# Revit family: 4C-6_Door_High_Units_FL.rfa
name_source: partatom
category: Specialty Equipment
revit_build: Autodesk Revit 2016 (Build: 20150714_1515(x64)
units: mm (PartAtom-declared; Revit-internal decimal feet)

## family parameters
Always vertical = Yes
Cut with Voids When Loaded = No
Host = Wall
Part Type = Normal
Room Calculation Point = No
Round Connector Dimension = Use Diameter
Shared = No

## types (13) — shared parameters
Assembly Code = C1030910
Back Enclosure Material = Aluminum - Salsbury Finish = Anodized
Depth = 17.025"
Door Slot R3 = 3700 Series 4C Door Configurations : Empty
Height = 23.470"
Latch Locks - Left Side = No
Latch Locks - Right Side = No
Lock Material = Stainless Steel -Salsbury Finish =  Polished
Manufacturer = Salsbury Industries
MasterFormat Number = 10 55 00
MasterFormat Title = Postal Specialties
Version = 2.0 (08/09/16)

## per-type parameters (varying)
| type | Bottom Back Plate | Description | Door Slot L1 | Door Slot L2 | Door Slot L3 | Door Slot L4 | Door Slot L5 | Door Slot L6 | Door Slot R1 | Door Slot R2 | Door Slot R4 | Door Slot R5 | Door Slot R6 | Latch Alignment | Left Inside Wall | Right Inside Wall | Top Back Plate | Type Comments | Vertical Center Divider | Width |
| 3706D-10 FL | Yes | 6 Door High Unit: 10 MB1, OM2 | 3700 Series 4C Door Configurations : MB1 Door | 3700 Series 4C Door Configurations : MB1 Door w/ Divider | 3700 Series 4C Door Configurations : MB1 Door w/ Divider | 3700 Series 4C Door Configurations : MB1 Door w/ Divider | 3700 Series 4C Door Configurations : MB1 Door w/ Divider | 3700 Series 4C Door Configurations : MB1 Door w/ Divider | 3700 Series 4C Door Configurations : MB1 Door | 3700 Series 4C Door Configurations : MB1 Door w/ Divider | 3700 Series 4C OM2 Configuration : OM2-FL | 3700 Series 4C Door Configurations : MB1 Door w/ Divider | 3700 Series 4C Door Configurations : MB1 Door w/ Divider | 14.857" | Yes | Yes | Yes | 4C Standard Horizontal Mailbox - Front Loading | Yes | 31.098" |
| 3706S-04 FL | No | 6 Door High Unit: 4 MB1, OM2 | 3700 Series 4C Door Configurations : Empty | 3700 Series 4C Door Configurations : Empty | 3700 Series 4C Door Configurations : Empty | 3700 Series 4C Door Configurations : Empty | 3700 Series 4C Door Configurations : Empty | 3700 Series 4C Door Configurations : Empty | 3700 Series 4C Door Configurations : MB1 Door | 3700 Series 4C Door Configurations : MB1 Door w/ Divider | 3700 Series 4C OM2 Configuration : OM2-FL | 3700 Series 4C Door Configurations : MB1 Door w/ Divider | 3700 Series 4C Door Configurations : MB1 Door w/ Divider | 13.876" | No | No | No | 4C Standard Horizontal Mailbox - Front Loading | No | 16.344" |
| 3706S-02 FL | No | 6 Door High Unit: 2 MB2, OM2 | 3700 Series 4C Door Configurations : Empty | 3700 Series 4C Door Configurations : Empty | 3700 Series 4C Door Configurations : Empty | 3700 Series 4C Door Configurations : Empty | 3700 Series 4C Door Configurations : Empty | 3700 Series 4C Door Configurations : Empty | 3700 Series 4C Door Configurations : Empty | 3700 Series 4C Door Configurations : MB2 Door | 3700 Series 4C OM2 Configuration : OM2-FL | 3700 Series 4C Door Configurations : Empty | 3700 Series 4C Door Configurations : MB2 Door w/ Divider | 13.876" | No | No | No | 4C Standard Horizontal Mailbox - Front Loading | No | 16.344" |
| 3706S-01 FL | No | 6 Door High Unit: 1 MB4, OM2 | 3700 Series 4C Door Configurations : Empty | 3700 Series 4C Door Configurations : Empty | 3700 Series 4C Door Configurations : Empty | 3700 Series 4C Door Configurations : Empty | 3700 Series 4C Door Configurations : Empty | 3700 Series 4C Door Configurations : Empty | 3700 Series 4C Door Configurations : Empty | 3700 Series 4C OM2 Configuration : OM2-FL | 3700 Series 4C Door Configurations : Empty | 3700 Series 4C Door Configurations : Empty | 3700 Series 4C Door Configurations : MB4 Door w/ Divider | 13.876" | No | No | No | 4C Standard Horizontal Mailbox - Front Loading | No | 16.344" |
| 3706S-1P FL | No | 6 Door High Unit: 1 PL6 | 3700 Series 4C Door Configurations : Empty | 3700 Series 4C Door Configurations : Empty | 3700 Series 4C Door Configurations : Empty | 3700 Series 4C Door Configurations : Empty | 3700 Series 4C Door Configurations : Empty | 3700 Series 4C Door Configurations : Empty | 3700 Series 4C Door Configurations : Empty | 3700 Series 4C Door Configurations : Empty | 3700 Series 4C Door Configurations : Empty | 3700 Series 4C Door Configurations : Empty | 3700 Series 4C Parcel Configurations : PL6 | 13.876" | No | No | No | 4C Standard Horizontal Mailbox - Front Loading | No | 16.344" |
| 3706D-09 FL | Yes | 6 Door High Unit: 9 MB1, OM3 | 3700 Series 4C Door Configurations : MB1 Door | 3700 Series 4C Door Configurations : MB1 Door w/ Divider | 3700 Series 4C Door Configurations : MB1 Door w/ Divider | 3700 Series 4C Door Configurations : MB1 Door w/ Divider | 3700 Series 4C Door Configurations : MB1 Door w/ Divider | 3700 Series 4C Door Configurations : MB1 Door w/ Divider | 3700 Series 4C Door Configurations : MB1 Door | 3700 Series 4C Door Configurations : MB1 Door w/ Divider | 3700 Series 4C Door Configurations : Empty | 3700 Series 4C OM3 Configuration : OM3-FL | 3700 Series 4C Door Configurations : MB1 Door w/ Divider | 14.857" | Yes | Yes | Yes | 4C Standard Horizontal Mailbox - Front Loading | Yes | 31.098" |
| 3706D-06 FL | Yes | 6 Door High Unit: 6 MB1, 1 PL4, OM2 | 3700 Series 4C Door Configurations : MB1 Door | 3700 Series 4C Door Configurations : MB1 Door w/ Divider | 3700 Series 4C Door Configurations : Empty | 3700 Series 4C Door Configurations : Empty | 3700 Series 4C Door Configurations : Empty | 3700 Series 4C Parcel Configurations : PL4 w/ Divider | 3700 Series 4C Door Configurations : MB1 Door | 3700 Series 4C Door Configurations : MB1 Door w/ Divider | 3700 Series 4C OM2 Configuration : OM2-FL | 3700 Series 4C Door Configurations : MB1 Door w/ Divider | 3700 Series 4C Door Configurations : MB1 Door w/ Divider | 14.857" | Yes | Yes | Yes | 4C Standard Horizontal Mailbox - Front Loading | Yes | 31.098" |
| 3706DA-05 FL | Yes | 6 Door High Unit: 5 MB1, 1 PL5, OM2 | 3700 Series 4C Door Configurations : MB1 Door | 3700 Series 4C Door Configurations : Empty | 3700 Series 4C Door Configurations : Empty | 3700 Series 4C Door Configurations : Empty | 3700 Series 4C Door Configurations : Empty | 3700 Series 4C Parcel Configurations : PL5 w/ Divider | 3700 Series 4C Door Configurations : MB1 Door | 3700 Series 4C Door Configurations : MB1 Door w/ Divider | 3700 Series 4C OM2 Configuration : OM2-FL | 3700 Series 4C Door Configurations : MB1 Door w/ Divider | 3700 Series 4C Door Configurations : MB1 Door w/ Divider | 14.857" | Yes | Yes | Yes | 4C Standard Horizontal Mailbox - Front Loading | Yes | 31.098" |
| 3706D-05 FL | Yes | 6 Door High Unit: 5 MB2, OM2 | 3700 Series 4C Door Configurations : Empty | 3700 Series 4C Door Configurations : MB2 Door | 3700 Series 4C Door Configurations : Empty | 3700 Series 4C Door Configurations : MB2 Door w/ Divider | 3700 Series 4C Door Configurations : Empty | 3700 Series 4C Door Configurations : MB2 Door w/ Divider | 3700 Series 4C Door Configurations : Empty | 3700 Series 4C Door Configurations : MB2 Door | 3700 Series 4C OM2 Configuration : OM2-FL | 3700 Series 4C Door Configurations : Empty | 3700 Series 4C Door Configurations : MB2 Door w/ Divider | 14.857" | Yes | Yes | Yes | 4C Standard Horizontal Mailbox - Front Loading | Yes | 31.098" |
| 3706D-04 FL | Yes | 6 Door High Unit: 4 MB1, 1 PL6, OM2 | 3700 Series 4C Door Configurations : Empty | 3700 Series 4C Door Configurations : Empty | 3700 Series 4C Door Configurations : Empty | 3700 Series 4C Door Configurations : Empty | 3700 Series 4C Door Configurations : Empty | 3700 Series 4C Parcel Configurations : PL6 | 3700 Series 4C Door Configurations : MB1 Door | 3700 Series 4C Door Configurations : MB1 Door w/ Divider | 3700 Series 4C OM2 Configuration : OM2-FL | 3700 Series 4C Door Configurations : MB1 Door w/ Divider | 3700 Series 4C Door Configurations : MB1 Door w/ Divider | 14.857" | Yes | Yes | Yes | 4C Standard Horizontal Mailbox - Front Loading | Yes | 31.098" |
| 3706D-02 FL | Yes | 6 Door High Unit: 2 MB2, 1 PL6, OM2 | 3700 Series 4C Door Configurations : Empty | 3700 Series 4C Door Configurations : Empty | 3700 Series 4C Door Configurations : Empty | 3700 Series 4C Door Configurations : Empty | 3700 Series 4C Door Configurations : Empty | 3700 Series 4C Parcel Configurations : PL6 | 3700 Series 4C Door Configurations : Empty | 3700 Series 4C Door Configurations : MB2 Door | 3700 Series 4C OM2 Configuration : OM2-FL | 3700 Series 4C Door Configurations : Empty | 3700 Series 4C Door Configurations : MB2 Door w/ Divider | 14.857" | Yes | Yes | Yes | 4C Standard Horizontal Mailbox - Front Loading | Yes | 31.098" |
| 3706D-2P FL | Yes | 6 Door High Unit: 2 PL6 | 3700 Series 4C Door Configurations : Empty | 3700 Series 4C Door Configurations : Empty | 3700 Series 4C Door Configurations : Empty | 3700 Series 4C Door Configurations : Empty | 3700 Series 4C Door Configurations : Empty | 3700 Series 4C Parcel Configurations : PL6 | 3700 Series 4C Door Configurations : Empty | 3700 Series 4C Door Configurations : Empty | 3700 Series 4C Door Configurations : Empty | 3700 Series 4C Door Configurations : Empty | 3700 Series 4C Parcel Configurations : PL6 | 14.857" | Yes | Yes | Yes | 4C Standard Horizontal Mailbox - Front Loading | Yes | 31.098" |
| 3706S-1B FL | No | 6 Door High Unit - 1 Receptacle Bin | 3700 Series 4C Door Configurations : Empty | 3700 Series 4C Door Configurations : Empty | 3700 Series 4C Door Configurations : Empty | 3700 Series 4C Door Configurations : Empty | 3700 Series 4C Door Configurations : Empty | 3700 Series 4C Door Configurations : Empty | 3700 Series 4C Door Configurations : Empty | 3700 Series 4C Door Configurations : Empty | 3700 Series 4C Door Configurations : Empty | 3700 Series 4C Door Configurations : Empty | 4C-6 Door High Receptacle | 13.876" | No | No | No | 4C Horizontal Receptacle Bin - Front Loading | No | 16.344" |

note: column(s) folded — value = type name in every type: Model

## geometry (parser evidence)
native form markers: Blend x18, Extrusion x9, Sweep x78
no freeform markers — native parametric forms only
